# Revit family: DU-951
name_source: partatom
category: Plumbing Fixtures
revit_build: Autodesk Revit Architecture 2012 (Build: 20110309_2315(x64)
units: mm (PartAtom-declared; Revit-internal decimal feet)

## types (1)
- DU-951
    Angle valve = 832-10
    Assembly Code = D2010
    CW Connection = Yes
    CWFU = 0
    Cartridge = S-950-1
    Connection tubes = C-M10X1/2
    Cost = 0 $
    Default Elevation = 0' - 0"
    Description = Single lever basin mixer with angle valves. ½” BSP female inlets
    Dura Handle = S-DU954-1
    HW Connection = Yes
    HWFU = 0
    Keynote = Basin mixer. ½” female iron 400mm long flexible inlets.

Basin mixer. ½” female iron 400mm long flexible inlets.
Basin mixer. ½” female iron 400mm long flexible inlets.

Basin mixer. ½” female iron 400mm long flexible inlets.
    Manufacturer = COBRA
    Material = Chrome_Polished
    Model = DU-951
    Range = Dura
    Type Comments = SANS 1480
    URL = http://www.cobra.co.za
    Vent Connection = No
    WFU = 0
    Waste Connection = No

## geometry (parser evidence)
native form markers: Blend x2
no freeform markers — native parametric forms only
